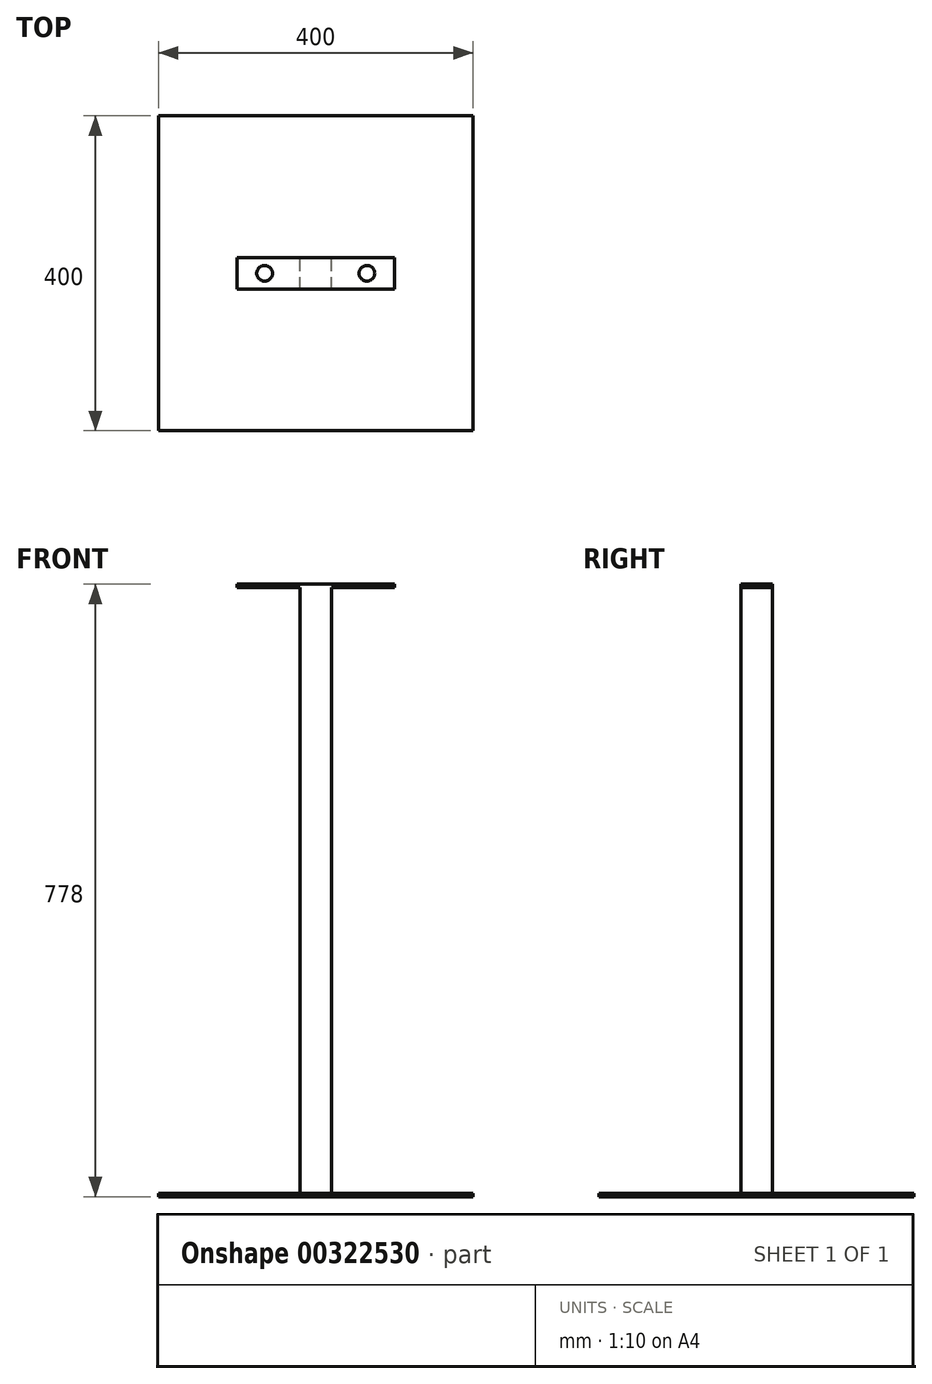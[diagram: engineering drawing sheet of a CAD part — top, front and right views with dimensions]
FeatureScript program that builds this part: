
annotation { "Feature Type Name" : "Feature", "Feature Type Description" : "" }
export const myFeature = defineFeature(function(context is Context, id is Id, definition is map)
    precondition{}
    {
        {
            var Q0;
            Q0=qCreatedBy(makeId("Top.planeOp"),FACE);
            var sketch = newSketch(context, id + "F0", { "sketchPlane" : qUnion([Q0])});
            skLineSegment(sketch, "E0.bottom", {"start": v(-200, -200) * mm, "end": v(200, -200) * mm});
            skLineSegment(sketch, "E0.top", {"start": v(-200, 200) * mm, "end": v(200, 200) * mm});
            skLineSegment(sketch, "E0.left", {"start": v(-200, -200) * mm, "end": v(-200, 200) * mm});
            skLineSegment(sketch, "E0.right", {"start": v(200, -200) * mm, "end": v(200, 200) * mm});
            skPoint(sketch, "E0.middle", {"position": v(0, 0) * mm});
            skSolve(sketch);
        }
        {
            var Q0;
            Q0=makeQuery(id+"F0.imprint","IMPRINT",FACE,{"disambiguationData":[TD([[makeQuery(id+"F0.imprint","IMPRINT",EDGE,{"derivedFrom":sQuery(id+"F0.wireOp",EDGE,"E0.bottom")}),1.0]])]});
            extrude(context, id + "F1", {"entities" : qUnion([Q0]), "depth" : 4 * mm});
        }
        {
            var Q0;
            Q0=makeQuery(id+"F1.opExtrude","CAP_FACE",FACE,{"disambiguationData":[OSD([sQuery(id+"F0.wireOp",EDGE,"E0.bottom"),sQuery(id+"F0.wireOp",EDGE,"E0.top"),sQuery(id+"F0.wireOp",EDGE,"E0.left"),sQuery(id+"F0.wireOp",EDGE,"E0.right")])],"isStart":false});
            var sketch = newSketch(context, id + "F2", { "sketchPlane" : qUnion([Q0])});
            skLineSegment(sketch, "E1.bottom", {"start": v(20, -20) * mm, "end": v(-20, -20) * mm});
            skLineSegment(sketch, "E1.top", {"start": v(20, 20) * mm, "end": v(-20, 20) * mm});
            skLineSegment(sketch, "E1.left", {"start": v(20, -20) * mm, "end": v(20, 20) * mm});
            skLineSegment(sketch, "E1.right", {"start": v(-20, -20) * mm, "end": v(-20, 20) * mm});
            skPoint(sketch, "E1.middle", {"position": v(0, 0) * mm});
            skSolve(sketch);
        }
        {
            var Q0;
            Q0=makeQuery(id+"F2.imprint","IMPRINT",FACE,{"disambiguationData":[TD([[makeQuery(id+"F2.imprint","IMPRINT",EDGE,{"derivedFrom":sQuery(id+"F2.wireOp",EDGE,"E1.bottom")}),-1.0]])]});
            extrude(context, id + "F3", {"entities" : qUnion([Q0]), "operationType" : NewBodyOperationType.ADD, "depth" : 770 * mm});
        }
        {
            var Q0;
            Q0=makeQuery(id+"F3.opExtrude","CAP_FACE",FACE,{"disambiguationData":[OSD([sQuery(id+"F2.wireOp",EDGE,"E1.bottom"),sQuery(id+"F2.wireOp",EDGE,"E1.top"),sQuery(id+"F2.wireOp",EDGE,"E1.left"),sQuery(id+"F2.wireOp",EDGE,"E1.right")])],"isStart":false});
            var sketch = newSketch(context, id + "F4", { "sketchPlane" : qUnion([Q0])});
            skLineSegment(sketch, "E2.bottom", {"start": v(100, 20) * mm, "end": v(-100, 20) * mm});
            skLineSegment(sketch, "E2.top", {"start": v(100, -20) * mm, "end": v(-100, -20) * mm});
            skLineSegment(sketch, "E2.left", {"start": v(100, 20) * mm, "end": v(100, -20) * mm});
            skLineSegment(sketch, "E2.right", {"start": v(-100, 20) * mm, "end": v(-100, -20) * mm});
            skPoint(sketch, "E2.middle", {"position": v(0, 0) * mm});
            skSolve(sketch);
        }
        {
            var Q0;
            Q0=qSketchRegion(id+"F4",true);
            extrude(context, id + "F5", {"entities" : qUnion([Q0]), "operationType" : NewBodyOperationType.ADD, "depth" : 4 * mm});
        }
        {
            var Q0;
            Q0=makeQuery(id+"F5.opExtrude","CAP_FACE",FACE,{"disambiguationData":[OSD([sQuery(id+"F4.wireOp",EDGE,"E2.bottom"),sQuery(id+"F4.wireOp",EDGE,"E2.top"),sQuery(id+"F4.wireOp",EDGE,"E2.left"),sQuery(id+"F4.wireOp",EDGE,"E2.right")])],"isStart":false});
            var sketch = newSketch(context, id + "F6", { "sketchPlane" : qUnion([Q0])});
            skCircle(sketch, "E3", {"center": v(-65, 0) * mm, "radius": 10 * mm});
            skSolve(sketch);
        }
        {
            var Q0;
            Q0=makeQuery(id+"F6.imprint","IMPRINT",FACE,{"disambiguationData":[TD([[makeQuery(id+"F6.imprint","IMPRINT",EDGE,{"derivedFrom":sQuery(id+"F6.wireOp",EDGE,"E3")}),-1.0]])]});
            var sketch = newSketch(context, id + "F7", { "sketchPlane" : qUnion([Q0])});
            skCircle(sketch, "E4", {"center": v(65, 0) * mm, "radius": 10 * mm});
            skSolve(sketch);
        }
        {
            var Q0;
            Q0=sQuery(id+"F6.wireOp",VERTEX,"E3.center");
            var Q1;
            Q1=makeQuery(id+"F1.opExtrude","SWEPT_BODY",BODY,{"disambiguationData":[OSD([sQuery(id+"F0.wireOp",EDGE,"E0.bottom"),sQuery(id+"F0.wireOp",EDGE,"E0.top"),sQuery(id+"F0.wireOp",EDGE,"E0.left"),sQuery(id+"F0.wireOp",EDGE,"E0.right")])]});
            hole(context, id + "F8", {"style" : HoleStyle.SIMPLE, "endStyle" : HoleEndStyle.BLIND, "holeDiameter" : 20 * mm, "holeDepth" : 20 * mm, "tappedDepth" : 12 * mm, "tapClearance" : 3, "startFromSketch" : true, "locations" : qUnion([Q0]), "scope" : qUnion([Q1])});
        }
        {
            var Q0;
            Q0=sQuery(id+"F7.wireOp",VERTEX,"E4.center");
            var Q1;
            Q1=makeQuery(id+"F1.opExtrude","SWEPT_BODY",BODY,{"disambiguationData":[OSD([sQuery(id+"F0.wireOp",EDGE,"E0.bottom"),sQuery(id+"F0.wireOp",EDGE,"E0.top"),sQuery(id+"F0.wireOp",EDGE,"E0.left"),sQuery(id+"F0.wireOp",EDGE,"E0.right")])]});
            hole(context, id + "F9", {"style" : HoleStyle.SIMPLE, "endStyle" : HoleEndStyle.BLIND, "holeDiameter" : 20 * mm, "holeDepth" : 20 * mm, "tappedDepth" : 12 * mm, "tapClearance" : 3, "startFromSketch" : true, "locations" : qUnion([Q0]), "scope" : qUnion([Q1])});
        }
    });
